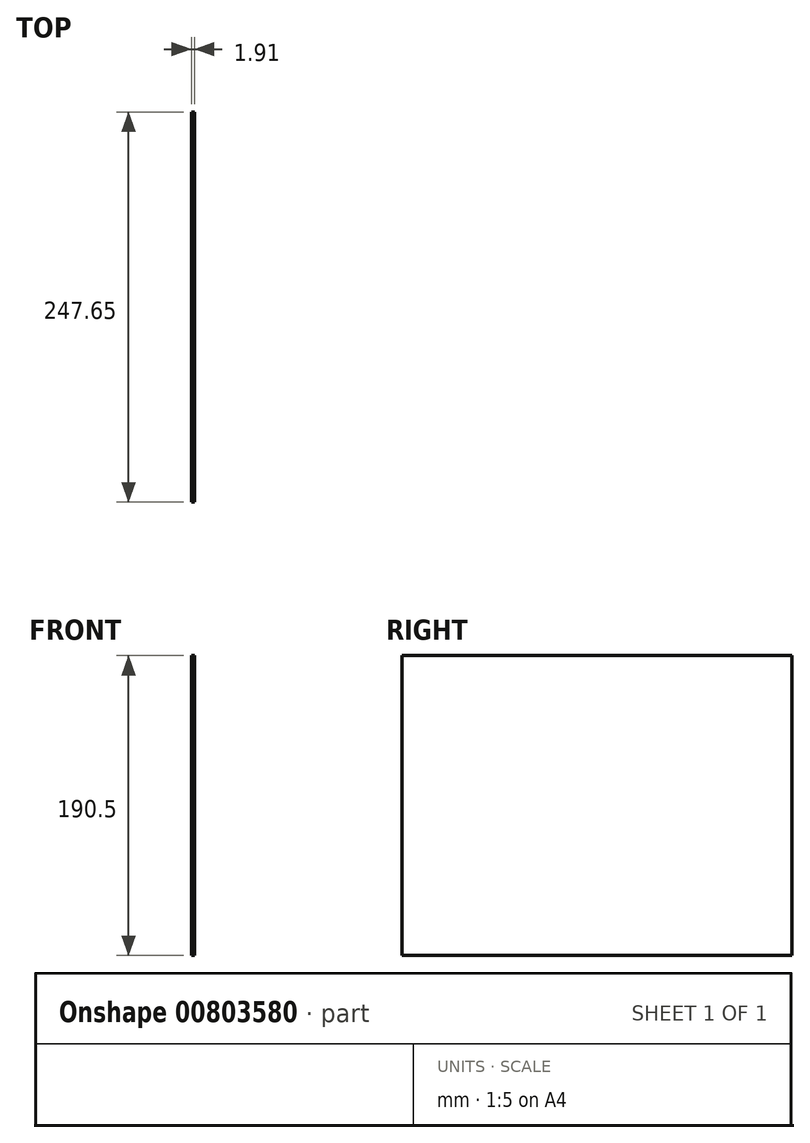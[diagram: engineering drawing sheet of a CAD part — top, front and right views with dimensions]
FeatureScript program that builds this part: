
annotation { "Feature Type Name" : "Feature", "Feature Type Description" : "" }
export const myFeature = defineFeature(function(context is Context, id is Id, definition is map)
    precondition{}
    {
        {
            var Q0;
            Q0=qCreatedBy(makeId("Right.planeOp"),FACE);
            var sketch = newSketch(context, id + "F0", { "sketchPlane" : qUnion([Q0])});
            skLineSegment(sketch, "E0.bottom", {"start": v(-124.16, 87.66) * mm, "end": v(123.49, 87.66) * mm});
            skLineSegment(sketch, "E0.top", {"start": v(-124.16, -102.84) * mm, "end": v(123.49, -102.84) * mm});
            skLineSegment(sketch, "E0.left", {"start": v(-124.16, 87.66) * mm, "end": v(-124.16, -102.84) * mm});
            skLineSegment(sketch, "E0.right", {"start": v(123.49, 87.66) * mm, "end": v(123.49, -102.84) * mm});
            skSolve(sketch);
        }
        {
            var Q0;
            Q0=makeQuery(id+"F0.imprint","IMPRINT",FACE,{"disambiguationData":[TD([[makeQuery(id+"F0.imprint","IMPRINT",EDGE,{"derivedFrom":sQuery(id+"F0.wireOp",EDGE,"E0.bottom")}),-1.0]])]});
            extrude(context, id + "F1", {"entities" : qUnion([Q0]), "depth" : 1.9 * mm, "offsetDistance" : 25.4 * mm});
        }
    });
